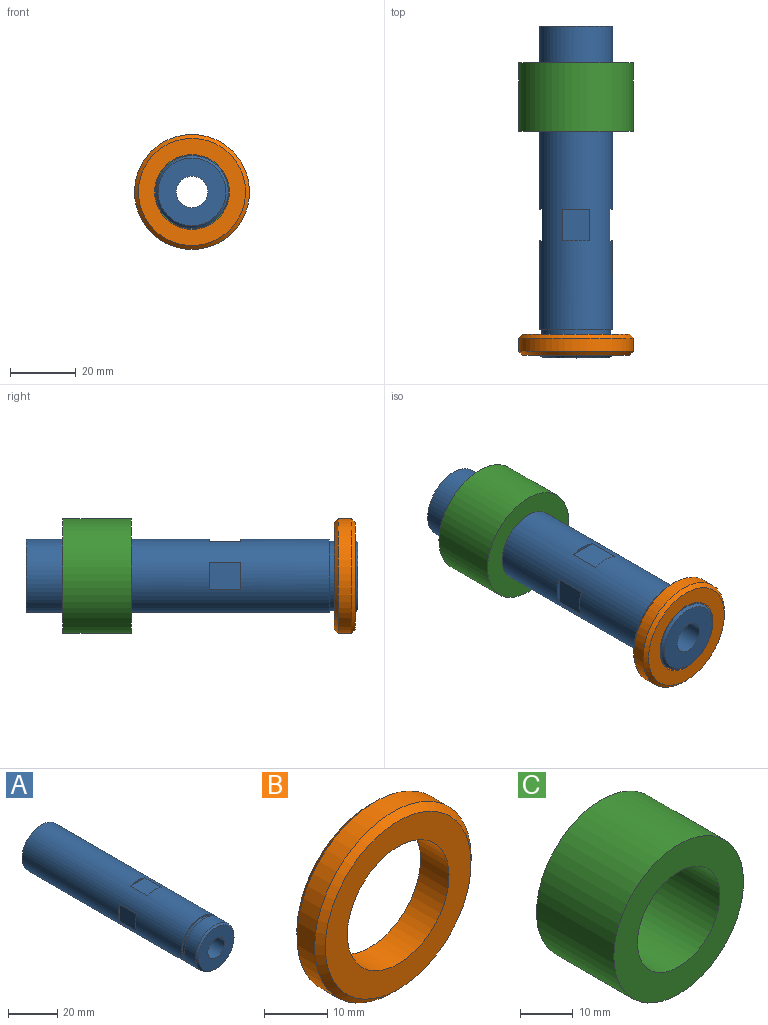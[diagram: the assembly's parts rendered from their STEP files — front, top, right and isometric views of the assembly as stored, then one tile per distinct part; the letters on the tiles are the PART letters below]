
ASSEMBLY  parts=3 mates=2
PART A: 19 faces, bbox 22.2x100.8x22.2 mm
  f0: plane 20.57x20.57mm, normal (0,-1,0), area 261.2mm2, adj f1,f9
  f1: cylinder r=4.76mm len=49.89mm, axis (0,-1,0), area 1492.9mm2, adj f0,f2
  f2: cone r=4.76mm half-angle=1.4deg, axis (0,1,0), area 1727.4mm2, adj f1,f3
  f3: plane 22.23x22.23mm, normal (0,1,0), area 273.6mm2, adj f2,f4
  f4: cylinder r=11.11mm len=92.09mm, axis (0,-1,0), area 6188.1mm2, adj f3,f5,f10,f11,f12,f13,f14,f15
  f5: plane 22.23x22.23mm, normal (0,-1,0), area 38.9mm2, adj f4,f6
  f6: cylinder r=10.54mm len=21.08mm, axis (0,-1,0), area 105.1mm2, adj f5,f7
  f7: plane 22.1x22.1mm, normal (0,1,0), area 34.5mm2, adj f6,f8
  f8: cylinder r=11.05mm len=22.1mm, axis (0,-1,0), area 442.6mm2, adj f7,f9
  f9: cone r=10.29mm half-angle=45deg, axis (0,1,0), area 72.2mm2, adj f0,f8
  f10: plane 8.26x0.8mm, normal (0,1,0), area 4.4mm2, adj f4,f11
  f11: plane 9.53x8.26mm, normal (0,0,1), area 78.6mm2, adj f4,f10,f12
  f12: plane 8.26x0.8mm, normal (0,-1,0), area 4.4mm2, adj f4,f11
  f13: plane 9.53x8.26mm, normal (1,0,0), area 78.6mm2, adj f4,f14,f15
  f14: plane 8.26x0.8mm, normal (0,1,0), area 4.4mm2, adj f4,f13
  f15: plane 8.26x0.8mm, normal (0,-1,0), area 4.4mm2, adj f4,f13
  f16: plane 8.26x0.8mm, normal (0,1,0), area 4.4mm2, adj f4,f17
  f17: plane 9.53x8.26mm, normal (-1,0,0), area 78.6mm2, adj f4,f16,f18
  f18: plane 8.26x0.8mm, normal (0,-1,0), area 4.4mm2, adj f4,f17
PART B: 6 faces, bbox 34.9x6.4x34.9 mm
  f0: cylinder r=11.35mm len=22.71mm, axis (0,1,0), area 453mm2, adj f2,f3
  f1: cylinder r=17.46mm len=34.93mm, axis (0,1,0), area 434.8mm2, adj f4,f5
  f2: plane 32.54x32.54mm, normal (0,-1,0), area 426.5mm2, adj f0,f4
  f3: plane 32.54x32.54mm, normal (0,1,0), area 426.5mm2, adj f0,f5
  f4: cone r=16.27mm half-angle=45deg, axis (0,1,0), area 178.9mm2, adj f1,f2
  f5: cone r=17.46mm half-angle=45deg, axis (0,-1,0), area 178.9mm2, adj f1,f3
PART C: 4 faces, bbox 34.9x20.8x34.9 mm
  f0: cylinder r=11.11mm len=22.23mm, axis (0,1,0), area 1454.3mm2, adj f2,f3
  f1: cylinder r=17.46mm len=34.93mm, axis (0,1,0), area 2285.3mm2, adj f2,f3
  f2: plane 34.93x34.93mm, normal (0,-1,0), area 570mm2, adj f0,f1
  f3: plane 34.93x34.93mm, normal (0,1,0), area 570mm2, adj f0,f1
PLACE A t=(0.73,-21.28,24.11)mm
PLACE B t=(0.73,-26.79,24.11)mm
PLACE C t=(0.73,55.72,24.11)mm
MATE fastened C.f0 <-> A.f1  axis (0,1,0) through (0.73,55.72,24.11)mm
MATE fastened B.f0 <-> A.f1  axis (0,1,0) through (0.73,-29.96,24.11)mm
